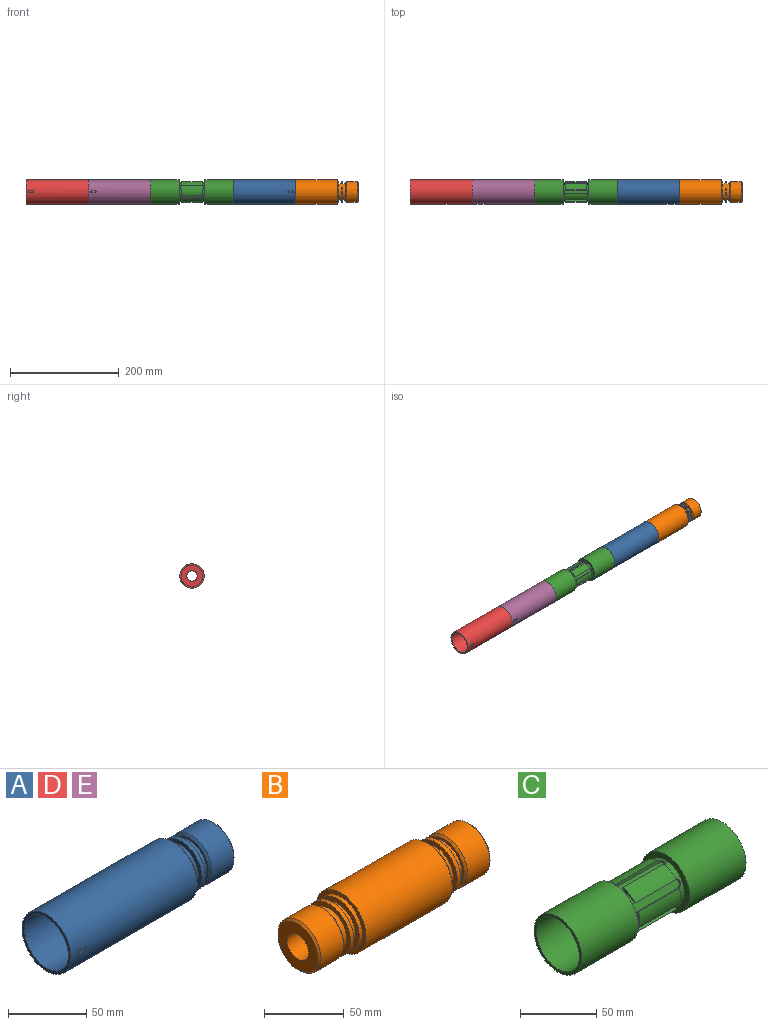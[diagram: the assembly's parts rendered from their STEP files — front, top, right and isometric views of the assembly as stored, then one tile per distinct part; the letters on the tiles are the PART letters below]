
ASSEMBLY  parts=5 mates=5
PART A: 23 faces, bbox 152.4x44.5x44.5 mm
  f0: cylinder r=19.05mm len=38.1mm, axis (1,0,0), area 2371.4mm2, adj f21,f22
  f1: cylinder r=22.23mm len=114.3mm, axis (1,0,0), area 15933.2mm2, adj f2,f8,f9,f10,f11,f12
  f2: plane 44.45x44.45mm, normal (-1,0,0), area 314.7mm2, adj f1,f3
  f3: cylinder r=19.84mm len=44.45mm, axis (1,0,0), area 5542.1mm2, adj f2,f4
  f4: plane 39.69x39.69mm, normal (-1,0,0), area 952.1mm2, adj f3,f5
  f5: cylinder r=9.53mm len=107.95mm, axis (1,0,0), area 6460.5mm2, adj f4,f6
  f6: plane 35.05x35.05mm, normal (1,0,0), area 680mm2, adj f5,f22
  f7: cylinder r=19.05mm len=38.1mm, axis (1,0,0), area 343.5mm2, adj f8,f18
  f8: plane 44.45x44.45mm, normal (1,0,0), area 411.7mm2, adj f1,f7
  f9: plane 6.35x0.96mm, normal (0,0,-1), area 6.1mm2, adj f1,f10,f12,f13
  f10: cylinder r=1.59mm len=3.18mm, axis (0,-1,0), area 4.9mm2, adj f1,f9,f11,f13
  f11: plane 6.35x0.96mm, normal (0,0,1), area 6.1mm2, adj f1,f10,f12,f13
  f12: cylinder r=1.59mm len=3.18mm, axis (0,-1,0), area 4.9mm2, adj f1,f9,f11,f13
  f13: plane 9.53x3.18mm, normal (0,-1,0), area 28.1mm2, adj f9,f10,f11,f12
  f14: plane 38.1x38.1mm, normal (1,0,0), area 385.9mm2, adj f15,f17
  f15: cylinder r=15.49mm len=30.99mm, axis (1,0,0), area 462.4mm2, adj f14,f16
  f16: plane 35.05x35.05mm, normal (-1,0,0), area 210.8mm2, adj f15,f21
  f17: cylinder r=19.05mm len=38.1mm, axis (1,0,0), area 343.5mm2, adj f14,f20
  f18: plane 38.1x38.1mm, normal (1,0,0), area 385.9mm2, adj f7,f19
  f19: cylinder r=15.49mm len=30.99mm, axis (1,0,0), area 462.4mm2, adj f18,f20
  f20: plane 38.1x38.1mm, normal (-1,0,0), area 385.9mm2, adj f17,f19
  f21: cone r=19.05mm half-angle=45deg, axis (1,0,0), area 247.7mm2, adj f0,f16
  f22: cone r=17.53mm half-angle=45deg, axis (-1,0,0), area 247.7mm2, adj f0,f6
PART B: 30 faces, bbox 152.4x44.5x44.5 mm
  f0: cylinder r=19.05mm len=38.1mm, axis (-1,0,0), area 2371.4mm2, adj f26,f27
  f1: cylinder r=19.05mm len=38.1mm, axis (-1,0,0), area 2371.4mm2, adj f24,f25
  f2: cylinder r=22.23mm len=76.2mm, axis (-1,0,0), area 10640.9mm2, adj f3,f9
  f3: plane 44.45x44.45mm, normal (-1,0,0), area 411.7mm2, adj f2,f4
  f4: cylinder r=19.05mm len=38.1mm, axis (-1,0,0), area 343.5mm2, adj f3,f22
  f5: plane 35.05x35.05mm, normal (-1,0,0), area 680mm2, adj f6,f27
  f6: cylinder r=9.53mm len=152.4mm, axis (-1,0,0), area 9120.7mm2, adj f5,f7
  f7: plane 35.05x35.05mm, normal (1,0,0), area 660.5mm2, adj f6,f24,f29
  f8: cylinder r=19.05mm len=38.1mm, axis (-1,0,0), area 343.5mm2, adj f9,f15
  f9: plane 44.45x44.45mm, normal (1,0,0), area 411.7mm2, adj f2,f8
  f10: plane 38.1x38.1mm, normal (1,0,0), area 385.9mm2, adj f11,f13
  f11: cylinder r=15.49mm len=30.99mm, axis (1,0,0), area 462.4mm2, adj f10,f12
  f12: plane 35.05x35.05mm, normal (-1,0,0), area 210.8mm2, adj f11,f25
  f13: cylinder r=19.05mm len=38.1mm, axis (-1,0,0), area 343.5mm2, adj f10,f14
  f14: plane 38.1x38.1mm, normal (-1,0,0), area 385.9mm2, adj f13,f16
  f15: plane 38.1x38.1mm, normal (1,0,0), area 385.9mm2, adj f8,f16
  f16: cylinder r=15.49mm len=30.99mm, axis (1,0,0), area 462.4mm2, adj f14,f15
  f17: plane 38.1x38.1mm, normal (-1,0,0), area 385.9mm2, adj f18,f20
  f18: cylinder r=15.49mm len=30.99mm, axis (-1,0,0), area 462.4mm2, adj f17,f19
  f19: plane 35.05x35.05mm, normal (1,0,0), area 210.8mm2, adj f18,f26
  f20: cylinder r=19.05mm len=38.1mm, axis (-1,0,0), area 343.5mm2, adj f17,f21
  f21: plane 38.1x38.1mm, normal (1,0,0), area 385.9mm2, adj f20,f23
  f22: plane 38.1x38.1mm, normal (-1,0,0), area 385.9mm2, adj f4,f23
  f23: cylinder r=15.49mm len=30.99mm, axis (-1,0,0), area 462.4mm2, adj f21,f22
  f24: cone r=19.05mm half-angle=45deg, axis (-1,0,0), area 247.7mm2, adj f1,f7
  f25: cone r=19.05mm half-angle=45deg, axis (1,0,0), area 247.7mm2, adj f1,f12
  f26: cone r=17.53mm half-angle=45deg, axis (-1,0,0), area 247.7mm2, adj f0,f19
  f27: cone r=17.53mm half-angle=45deg, axis (1,0,0), area 247.7mm2, adj f0,f5
  f28: cone r=0mm half-angle=59deg, axis (1,0,0), area 22.7mm2, adj f29
  f29: cylinder r=2.49mm len=6.35mm, axis (1,0,0), area 99.3mm2, adj f7,f28
PART C: 61 faces, bbox 152.4x44.5x44.5 mm
  f0: plane 11.3x7.22mm, normal (1,0,0), area 17.2mm2, adj f22,f40,f45,f58
  f1: plane 11.3x7.22mm, normal (1,0,0), area 17.2mm2, adj f22,f44,f49,f57
  f2: plane 13.05x2.36mm, normal (1,0,0), area 17.2mm2, adj f22,f48,f53,f55
  f3: plane 11.3x7.22mm, normal (1,0,0), area 17.2mm2, adj f22,f33,f52,f56
  f4: plane 11.3x7.22mm, normal (1,0,0), area 17.2mm2, adj f22,f32,f37,f60
  f5: plane 13.05x2.36mm, normal (1,0,0), area 17.2mm2, adj f22,f36,f41,f59
  f6: plane 11.3x7.22mm, normal (-1,0,0), area 17.2mm2, adj f24,f40,f45,f58
  f7: plane 11.3x7.22mm, normal (-1,0,0), area 17.2mm2, adj f24,f44,f49,f57
  f8: plane 13.05x2.36mm, normal (-1,0,0), area 17.2mm2, adj f24,f48,f53,f55
  f9: plane 11.3x7.22mm, normal (-1,0,0), area 17.2mm2, adj f24,f33,f52,f56
  f10: plane 11.3x7.22mm, normal (-1,0,0), area 17.2mm2, adj f24,f32,f37,f60
  f11: plane 13.05x2.36mm, normal (-1,0,0), area 17.2mm2, adj f24,f36,f41,f59
  f12: cylinder r=22.23mm len=52.39mm, axis (1,0,0), area 7315.6mm2, adj f17,f21
  f13: cylinder r=22.23mm len=52.39mm, axis (1,0,0), area 7315.6mm2, adj f18,f23
  f14: cylinder r=12.7mm len=63.5mm, axis (1,0,0), area 5067.1mm2, adj f15,f20
  f15: plane 39.69x39.69mm, normal (1,0,0), area 730.4mm2, adj f14,f16
  f16: cylinder r=19.84mm len=44.45mm, axis (1,0,0), area 5542.1mm2, adj f15,f17
  f17: plane 44.45x44.45mm, normal (1,0,0), area 314.7mm2, adj f12,f16
  f18: plane 44.45x44.45mm, normal (-1,0,0), area 314.7mm2, adj f13,f19
  f19: cylinder r=19.84mm len=44.45mm, axis (1,0,0), area 5542.1mm2, adj f18,f20
  f20: plane 39.69x39.69mm, normal (-1,0,0), area 730.4mm2, adj f14,f19
  f21: plane 44.45x44.45mm, normal (-1,0,0), area 593.8mm2, adj f12,f22
  f22: cylinder r=17.46mm len=34.93mm, axis (1,0,0), area 427.1mm2, adj f0,f1,f2,f3,f4,f5,f21,f31
  f23: plane 44.45x44.45mm, normal (1,0,0), area 593.8mm2, adj f13,f24
  f24: cylinder r=17.46mm len=34.93mm, axis (1,0,0), area 427.1mm2, adj f6,f7,f8,f9,f10,f11,f23,f34
  f25: plane 44.45x6.35mm, normal (0,0,1), area 273.6mm2, adj f43,f44,f45,f46
  f26: plane 44.45x5.5mm, normal (0,0.87,0.5), area 273.6mm2, adj f47,f48,f49,f50
  f27: plane 44.45x5.5mm, normal (0,0.87,-0.5), area 273.6mm2, adj f51,f52,f53,f54
  f28: plane 44.45x6.35mm, normal (0,0,-1), area 273.6mm2, adj f31,f32,f33,f34
  f29: plane 44.45x5.5mm, normal (0,-0.87,-0.5), area 273.6mm2, adj f35,f36,f37,f38
  f30: plane 44.45x5.5mm, normal (0,-0.87,0.5), area 273.6mm2, adj f39,f40,f41,f42
  f31: cylinder r=3.17mm len=6.35mm, axis (0,0,-1), area 14.4mm2, adj f22,f28,f32,f33
  f32: plane 38.1x2.68mm, normal (0,1,0), area 102mm2, adj f4,f10,f28,f31,f34,f60
  f33: plane 38.1x2.68mm, normal (0,-1,0), area 102mm2, adj f3,f9,f28,f31,f34,f56
  f34: cylinder r=3.17mm len=6.35mm, axis (0,0,-1), area 14.4mm2, adj f24,f28,f32,f33
  f35: cylinder r=3.17mm len=6.29mm, axis (0,-0.87,-0.5), area 14.4mm2, adj f22,f29,f36,f37
  f36: plane 38.1x2.32mm, normal (0,0.5,-0.87), area 102mm2, adj f5,f11,f29,f35,f38,f59
  f37: plane 38.1x2.32mm, normal (0,-0.5,0.87), area 102mm2, adj f4,f10,f29,f35,f38,f60
  f38: cylinder r=3.17mm len=6.29mm, axis (0,-0.87,-0.5), area 14.4mm2, adj f24,f29,f36,f37
  f39: cylinder r=3.17mm len=6.29mm, axis (0,-0.87,0.5), area 14.4mm2, adj f22,f30,f40,f41
  f40: plane 38.1x2.32mm, normal (0,-0.5,-0.87), area 102mm2, adj f0,f6,f30,f39,f42,f58
  f41: plane 38.1x2.32mm, normal (0,0.5,0.87), area 102mm2, adj f5,f11,f30,f39,f42,f59
  f42: cylinder r=3.17mm len=6.29mm, axis (0,-0.87,0.5), area 14.4mm2, adj f24,f30,f40,f41
  f43: cylinder r=3.17mm len=6.35mm, axis (0,0,1), area 14.4mm2, adj f22,f25,f44,f45
  f44: plane 38.1x2.68mm, normal (0,-1,0), area 102mm2, adj f1,f7,f25,f43,f46,f57
  f45: plane 38.1x2.68mm, normal (0,1,0), area 102mm2, adj f0,f6,f25,f43,f46,f58
  f46: cylinder r=3.17mm len=6.35mm, axis (0,0,1), area 14.4mm2, adj f24,f25,f44,f45
  f47: cylinder r=3.17mm len=6.29mm, axis (0,0.87,0.5), area 14.4mm2, adj f22,f26,f48,f49
  f48: plane 38.1x2.32mm, normal (0,-0.5,0.87), area 102mm2, adj f2,f8,f26,f47,f50,f55
  f49: plane 38.1x2.32mm, normal (0,0.5,-0.87), area 102mm2, adj f1,f7,f26,f47,f50,f57
  f50: cylinder r=3.17mm len=6.29mm, axis (0,0.87,0.5), area 14.4mm2, adj f24,f26,f48,f49
  f51: cylinder r=3.17mm len=6.29mm, axis (0,0.87,-0.5), area 14.4mm2, adj f22,f27,f52,f53
  f52: plane 38.1x2.32mm, normal (0,0.5,0.87), area 102mm2, adj f3,f9,f27,f51,f54,f56
  f53: plane 38.1x2.32mm, normal (0,-0.5,-0.87), area 102mm2, adj f2,f8,f27,f51,f54,f55
  f54: cylinder r=3.17mm len=6.29mm, axis (0,0.87,-0.5), area 14.4mm2, adj f24,f27,f52,f53
  f55: cylinder r=18.82mm len=38.1mm, axis (1,0,0), area 507.9mm2, adj f2,f8,f48,f53
  f56: cylinder r=18.82mm len=38.1mm, axis (1,0,0), area 507.9mm2, adj f3,f9,f33,f52
  f57: cylinder r=18.82mm len=38.1mm, axis (1,0,0), area 507.9mm2, adj f1,f7,f44,f49
  f58: cylinder r=18.82mm len=38.1mm, axis (1,0,0), area 507.9mm2, adj f0,f6,f40,f45
  f59: cylinder r=18.82mm len=38.1mm, axis (1,0,0), area 507.9mm2, adj f5,f11,f36,f41
  f60: cylinder r=18.82mm len=38.1mm, axis (1,0,0), area 507.9mm2, adj f4,f10,f32,f37
PART D: same geometry as A
PART E: same geometry as A
PLACE A rot(axis=(0,-1,0.01),180deg) t=(307.42,-16.9,19.12)mm
PLACE B rot(axis=(1,0,0),88.5deg) t=(345.52,-16.9,19.12)mm
PLACE C rot(axis=(-1,0,0),1.5deg) t=(116.92,-16.9,19.12)mm fixed
PLACE D rot(axis=(-1,0,0),1.5deg) t=(-187.88,-16.9,19.12)mm
PLACE E rot(axis=(-1,0,0),1.5deg) t=(-73.58,-16.9,19.12)mm
MATE fastened E.f0 <-> C.f12  axis (1,0,0) through (40.72,-16.9,19.12)mm
MATE cylindrical A.f0 <-> B.f24  axis (1,0,0) through (307.42,-16.9,19.12)mm
MATE revolute C.f12 <-> A.f0  axis (1,0,0) through (193.12,-16.9,19.12)mm
MATE parallel A.f9 <-> E.f11  axis (0,0.03,1) through (297.9,-38.63,18.11)mm
MATE fastened E.f0 <-> D.f0  axis (1,0,0) through (-73.58,-16.9,19.12)mm
